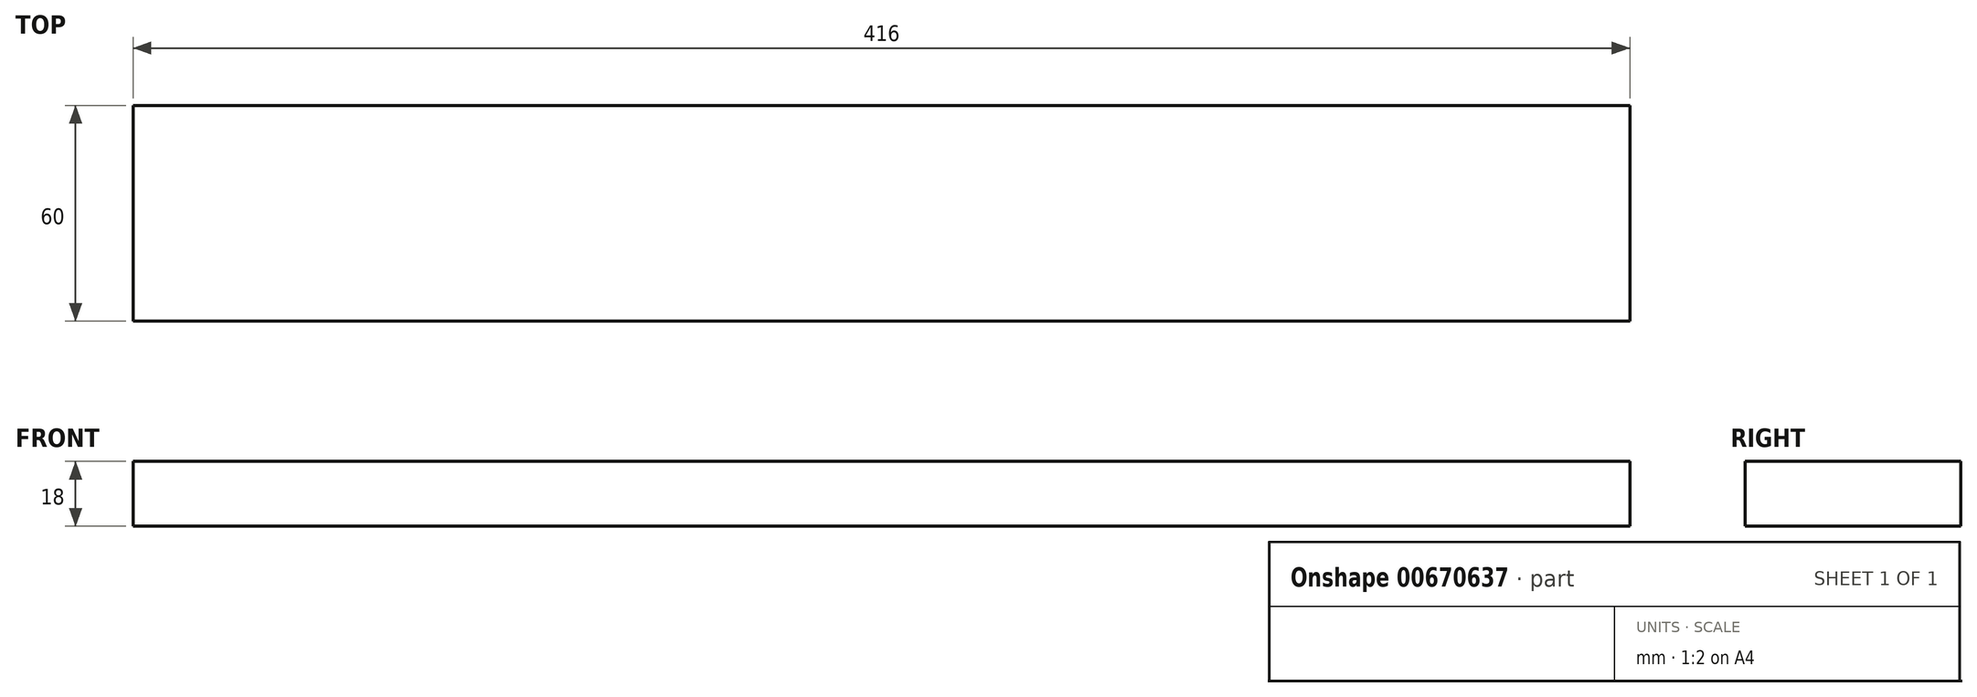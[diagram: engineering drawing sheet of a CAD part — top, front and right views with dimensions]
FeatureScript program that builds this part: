
annotation { "Feature Type Name" : "Feature", "Feature Type Description" : "" }
export const myFeature = defineFeature(function(context is Context, id is Id, definition is map)
    precondition{}
    {
        {
            var Q0;
            Q0=qCreatedBy(makeId("Top.planeOp"),FACE);
            var sketch = newSketch(context, id + "F0", { "sketchPlane" : qUnion([Q0])});
            skLineSegment(sketch, "E0.bottom", {"start": v(208, 30) * mm, "end": v(-208, 30) * mm});
            skLineSegment(sketch, "E0.top", {"start": v(208, -30) * mm, "end": v(-208, -30) * mm});
            skLineSegment(sketch, "E0.left", {"start": v(208, 30) * mm, "end": v(208, -30) * mm});
            skLineSegment(sketch, "E0.right", {"start": v(-208, 30) * mm, "end": v(-208, -30) * mm});
            skPoint(sketch, "E0.middle", {"position": v(0, 0) * mm});
            skSolve(sketch);
        }
        {
            var Q0;
            Q0 = qSketchRegion(id + "F0", true);
            extrude(context, id + "F1", {"entities" : qUnion([Q0]), "endBound" : BoundingType.SYMMETRIC, "depth" : 18 * mm, "offsetDistance" : 25 * mm});
        }
    });
